# Revit family: Shower-Valve_Trim-KOHLER-Composed-K-22785IN
name_source: partatom
category: Plumbing Fixtures
units: mm (PartAtom-declared; Revit-internal decimal feet)

## family parameters
Cut with Voids When Loaded = No
Host = Face
OmniClass Number = 23.31.25.00
OmniClass Title = Toilet and Bath Specialties
Part Type = Normal
Room Calculation Point = No
Round Connector Dimension = Use Diameter
Shared = No

## types (2) — shared parameters
ADA Compliant = No
CW Connection = Yes
Cold Water Inlet = Cold Water Inlet
Date Modified = 12/05/2022
Description = 40mm RBS Trim + AT235 Valve
Drain Included = No
Flow Rate = 0 GPM
HW Connection = Yes
Handle Clearance = 2 15/16"
Height = 6 9/16"
Hot Water Inlet = Hot Water Inlet
Length = 3 9/16"
Manufacturer = Kohler Co.
Master Format 2014 = 22 42 23
Master Format 2014 Name = Residential Showers
Material = Premium Metal Construction
Pressure = 0.00 psi
Product Name = Composed
Tempered Water Inlet 1 = Tempered Water Inlet 1
Tempered Water Inlet 2 = Tempered Water Inlet 2
URL = https://www.kohler.co.in
Vent Connection = No
Waste Connection = No
Waste Water Outlet = Waste Water Outlet
WaterSense Certified = No
Width = 4 7/16"

## per-type parameters (varying)
| type | Assembly Code | Default Elevation | Finish | Model | Type |
| BV-Brushed Bronze | D2010700 | 42" | Kohler-Metal-BV-Brushed_Bronze | K-22785IN-4-BV | 1 |
| RGD-Polished Rose Gold | D2020 | 36" | Kohler-Metal-RGD-Polished_Rose_Gold | K-22785IN-4-RGD | 2 |

## geometry (parser evidence)
native form markers: Sweep x5
no freeform markers — native parametric forms only
